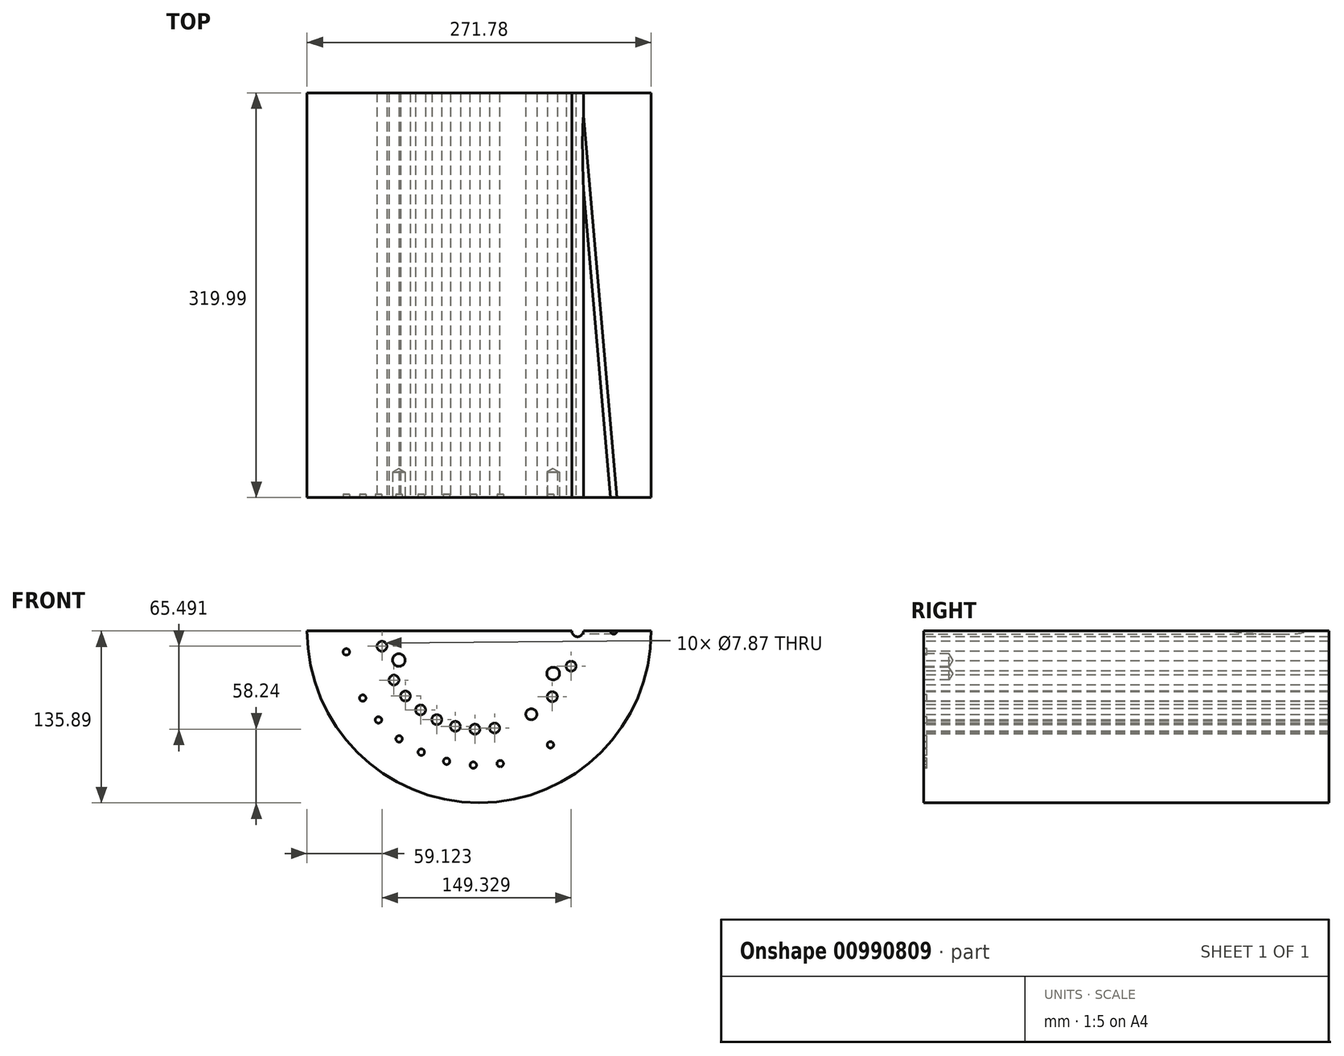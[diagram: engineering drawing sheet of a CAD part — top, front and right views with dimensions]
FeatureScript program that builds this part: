
annotation { "Feature Type Name" : "Feature", "Feature Type Description" : "" }
export const myFeature = defineFeature(function(context is Context, id is Id, definition is map)
    precondition{}
    {
        {
            var Q0;
            Q0=qCreatedBy(makeId("Front.planeOp"),FACE);
            var sketch = newSketch(context, id + "F0", { "sketchPlane" : qUnion([Q0])});
            skCircle(sketch, "E0", {"center": v(0, 0) * mm, "radius": 135.9 * mm});
            skSolve(sketch);
        }
        {
            var Q0;
            Q0 = qSketchRegion(id + "F0", true);
            var Q1;
            Q1 = qSketchRegion(id + "F21", true);
            extrude(context, id + "F1", {"entities" : qUnion([Q0, Q1]), "depth" : 1289.3 * mm, "offsetDistance" : 25.4 * mm});
        }
        {
            var Q0;
            Q0=makeQuery(id+"F1.opExtrude","CAP_FACE",FACE,{"disambiguationData":[OSD([sQuery(id+"F0.wireOp",EDGE,"E0")])],"isStart":false});
            var sketch = newSketch(context, id + "F2", { "sketchPlane" : qUnion([Q0])});
            skCircle(sketch, "E1", {"center": v(0, 0) * mm, "radius": 87.38 * mm});
            skSolve(sketch);
        }
        {
            var Q0;
            Q0 = qSketchRegion(id + "F2", true);
            extrude(context, id + "F3", {"entities" : qUnion([Q0]), "operationType" : NewBodyOperationType.REMOVE, "oppositeDirection" : true, "depth" : 120.65 * mm, "offsetDistance" : 25.4 * mm});
        }
        {
            var Q0;
            Q0=makeQuery(id+"F1.opExtrude","CAP_FACE",FACE,{"disambiguationData":[OSD([sQuery(id+"F0.wireOp",EDGE,"E0")])],"isStart":false});
            var sketch = newSketch(context, id + "F4", { "sketchPlane" : qUnion([Q0])});
            skCircle(sketch, "E2", {"center": v(0, 0) * mm, "radius": 89.66 * mm});
            skSolve(sketch);
        }
        {
            var Q0;
            Q0 = qSketchRegion(id + "F4", true);
            extrude(context, id + "F5", {"entities" : qUnion([Q0]), "operationType" : NewBodyOperationType.REMOVE, "oppositeDirection" : true, "depth" : 25.4 * mm, "offsetDistance" : 25.4 * mm});
        }
        {
            var Q0;
            Q0=makeQuery(id+"F3.boolean.opBoolean","COPY",EDGE,{"derivedFrom":makeQuery(id+"F3.opExtrude","CAP_EDGE",EDGE,{"disambiguationData":[OSD([sQuery(id+"F2.wireOp",EDGE,"E1")])],"isStart":false})});
            var Q1;
            Q1=makeQuery(id+"F5.boolean.opBoolean","COPY",EDGE,{"derivedFrom":makeQuery(id+"F5.opExtrude","CAP_EDGE",EDGE,{"disambiguationData":[OSD([sQuery(id+"F4.wireOp",EDGE,"E2")])],"isStart":false})});
            fillet(context, id + "F6", {"entities" : qUnion([Q0, Q1]), "radius" : 3.05 * mm, "tangentPropagation" : true, "allowEdgeOverflow" : false});
        }
        {
            var Q0;
            Q0=makeQuery(id+"F3.boolean.opBoolean","COPY",FACE,{"derivedFrom":makeQuery(id+"F3.opExtrude","CAP_FACE",FACE,{"disambiguationData":[OSD([sQuery(id+"F2.wireOp",EDGE,"E1")])],"isStart":false})});
            var sketch = newSketch(context, id + "F7", { "sketchPlane" : qUnion([Q0])});
            skPoint(sketch, "E3", {"position": v(71.61, 0) * mm});
            skPoint(sketch, "E4", {"position": v(32.51, 63.8) * mm});
            skPoint(sketch, "E5", {"position": v(-18.87, 69.08) * mm});
            skPoint(sketch, "E6", {"position": v(-65.18, 42.33) * mm});
            skPoint(sketch, "E7", {"position": v(-70.05, 14.89) * mm});
            skPoint(sketch, "E8", {"position": v(66.86, -25.66) * mm});
            skPoint(sketch, "E9", {"position": v(66.86, 25.66) * mm});
            skPoint(sketch, "E10", {"position": v(53.22, -47.92) * mm});
            skPoint(sketch, "E11", {"position": v(37.95, -60.73) * mm});
            skPoint(sketch, "E12", {"position": v(11.2, -70.73) * mm});
            skPoint(sketch, "E13", {"position": v(-3.12, -71.55) * mm});
            skPoint(sketch, "E14", {"position": v(-17.32, -69.49) * mm});
            skPoint(sketch, "E15", {"position": v(-30.83, -64.64) * mm});
            skPoint(sketch, "E16", {"position": v(-42.37, -57.2) * mm});
            skPoint(sketch, "E17", {"position": v(-53.64, -47.45) * mm});
            skPoint(sketch, "E18", {"position": v(-62.02, -35.8) * mm});
            skPoint(sketch, "E19", {"position": v(-70.73, -11.2) * mm});
            skCircle(sketch, "E20", {"center": v(-65.18, 42.33) * mm, "radius": 3.94 * mm});
            skCircle(sketch, "E21", {"center": v(0, 0) * mm, "radius": 77.72 * mm, "construction": true});
            skLineSegment(sketch, "E22", {"start": v(0, 0) * mm, "end": v(-20.48, 74.98) * mm, "construction": true});
            skLineSegment(sketch, "E23", {"start": v(0, 0) * mm, "end": v(-45.99, 62.66) * mm, "construction": true});
            skLineSegment(sketch, "E24", {"start": v(0, 0) * mm, "end": v(-76.03, 16.16) * mm, "construction": true});
            skLineSegment(sketch, "E25", {"start": v(0, 0) * mm, "end": v(-76.77, -12.16) * mm, "construction": true});
            skLineSegment(sketch, "E26", {"start": v(0, 0) * mm, "end": v(35.29, 69.25) * mm, "construction": true});
            skLineSegment(sketch, "E27", {"start": v(0, 0) * mm, "end": v(72.56, 27.85) * mm, "construction": true});
            skLineSegment(sketch, "E28", {"start": v(0, 0) * mm, "end": v(77.72, 0) * mm, "construction": true});
            skLineSegment(sketch, "E29", {"start": v(0, 0) * mm, "end": v(72.56, -27.85) * mm, "construction": true});
            skLineSegment(sketch, "E30", {"start": v(0, 0) * mm, "end": v(57.76, -52) * mm, "construction": true});
            skLineSegment(sketch, "E31", {"start": v(0, 0) * mm, "end": v(41.19, -65.91) * mm, "construction": true});
            skLineSegment(sketch, "E32", {"start": v(0, 0) * mm, "end": v(12.16, -76.77) * mm, "construction": true});
            skLineSegment(sketch, "E33", {"start": v(0, 0) * mm, "end": v(-3.4, -77.65) * mm, "construction": true});
            skLineSegment(sketch, "E34", {"start": v(0, 0) * mm, "end": v(-18.8, -75.42) * mm, "construction": true});
            skLineSegment(sketch, "E35", {"start": v(0, 0) * mm, "end": v(-33.46, -70.15) * mm, "construction": true});
            skLineSegment(sketch, "E36", {"start": v(0, 0) * mm, "end": v(-46.27, -62.45) * mm, "construction": true});
            skLineSegment(sketch, "E37", {"start": v(0, 0) * mm, "end": v(-58.21, -51.5) * mm, "construction": true});
            skLineSegment(sketch, "E38", {"start": v(0, 0) * mm, "end": v(-67.31, -38.86) * mm, "construction": true});
            skCircle(sketch, "E39", {"center": v(-45.99, 62.66) * mm, "radius": 3.94 * mm});
            skCircle(sketch, "E40", {"center": v(-20.48, 74.98) * mm, "radius": 3.94 * mm});
            skCircle(sketch, "E41", {"center": v(35.29, 69.25) * mm, "radius": 3.94 * mm});
            skCircle(sketch, "E42", {"center": v(72.56, 27.85) * mm, "radius": 3.94 * mm});
            skCircle(sketch, "E43", {"center": v(77.72, 0) * mm, "radius": 4.64 * mm});
            skCircle(sketch, "E44", {"center": v(72.56, -27.85) * mm, "radius": 3.94 * mm});
            skCircle(sketch, "E45", {"center": v(57.76, -52) * mm, "radius": 3.94 * mm});
            skCircle(sketch, "E46", {"center": v(41.19, -65.91) * mm, "radius": 4.38 * mm});
            skCircle(sketch, "E47", {"center": v(12.16, -76.77) * mm, "radius": 3.94 * mm});
            skCircle(sketch, "E48", {"center": v(-3.4, -77.65) * mm, "radius": 3.94 * mm});
            skCircle(sketch, "E49", {"center": v(-18.8, -75.42) * mm, "radius": 3.94 * mm});
            skCircle(sketch, "E50", {"center": v(-33.46, -70.15) * mm, "radius": 3.94 * mm});
            skCircle(sketch, "E51", {"center": v(-46.27, -62.45) * mm, "radius": 3.94 * mm});
            skCircle(sketch, "E52", {"center": v(-58.21, -51.5) * mm, "radius": 3.94 * mm});
            skCircle(sketch, "E53", {"center": v(-67.31, -38.86) * mm, "radius": 3.94 * mm});
            skCircle(sketch, "E54", {"center": v(-76.77, -12.16) * mm, "radius": 3.94 * mm});
            skCircle(sketch, "E55", {"center": v(-76.03, 16.16) * mm, "radius": 3.94 * mm});
            skSolve(sketch);
        }
        {
            var Q0;
            Q0 = qSketchRegion(id + "F7", true);
            extrude(context, id + "F8", {"entities" : qUnion([Q0]), "operationType" : NewBodyOperationType.REMOVE, "oppositeDirection" : true, "depth" : 762 * mm, "offsetDistance" : 25.4 * mm});
        }
        {
            var Q0;
            Q0 = qSketchRegion(id + "F7", true);
            extrude(context, id + "F9", {"entities" : qUnion([Q0]), "operationType" : NewBodyOperationType.REMOVE, "oppositeDirection" : true, "depth" : 762 * mm, "offsetDistance" : 25.4 * mm});
        }
        {
            var Q0;
            Q0=makeQuery(id+"F1.opExtrude","CAP_FACE",FACE,{"disambiguationData":[OSD([sQuery(id+"F0.wireOp",EDGE,"E0")])],"isStart":false});
            var sketch = newSketch(context, id + "F10", { "sketchPlane" : qUnion([Q0])});
            skCircle(sketch, "E56", {"center": v(0, 0) * mm, "radius": 50 * mm});
            skCircle(sketch, "E57", {"center": v(0, 0) * mm, "radius": 165.87 * mm});
            skSolve(sketch);
        }
        {
            var Q0;
            Q0 = qSketchRegion(id + "F10", true);
            extrude(context, id + "F11", {"entities" : qUnion([Q0]), "operationType" : NewBodyOperationType.REMOVE, "oppositeDirection" : true, "depth" : 120.65 * mm, "offsetDistance" : 25.4 * mm});
        }
        {
            var Q0;
            Q0 = qSketchRegion(id + "F7", true);
            extrude(context, id + "F12", {"entities" : qUnion([Q0]), "operationType" : NewBodyOperationType.REMOVE, "oppositeDirection" : true, "depth" : 25.4 * mm, "offsetDistance" : 25.4 * mm});
        }
        {
            var Q0;
            Q0=makeQuery(id+"F11.boolean.opBoolean","MERGE",FACE,{"derivedFrom":[makeQuery(id+"F3.boolean.opBoolean","COPY",FACE,{"derivedFrom":makeQuery(id+"F3.opExtrude","CAP_FACE",FACE,{"disambiguationData":[OSD([sQuery(id+"F2.wireOp",EDGE,"E1")])],"isStart":false})})],"fromTools":[makeQuery(id+"F11.opExtrude","CAP_FACE",FACE,{"disambiguationData":[OSD([sQuery(id+"F10.wireOp",EDGE,"E56"),sQuery(id+"F10.wireOp",EDGE,"E57")])],"isStart":false})]});
            var sketch = newSketch(context, id + "F13", { "sketchPlane" : qUnion([Q0])});
            skCircle(sketch, "E58", {"center": v(0, 0) * mm, "radius": 67.5 * mm});
            skPoint(sketch, "E59", {"position": v(0, 67.5) * mm});
            skPoint(sketch, "E60", {"position": v(58.46, -33.75) * mm});
            skPoint(sketch, "E61", {"position": v(-63.43, -23.09) * mm});
            skLineSegment(sketch, "E62", {"start": v(-63.43, -23.09) * mm, "end": v(0, 0) * mm});
            skLineSegment(sketch, "E63", {"start": v(0, 0) * mm, "end": v(0, 67.5) * mm});
            skLineSegment(sketch, "E64", {"start": v(0, 0) * mm, "end": v(58.46, -33.75) * mm});
            skSolve(sketch);
        }
        {
            var Q0;
            Q0=sQuery(id+"F13.wireOp",VERTEX,"E59");
            var Q1;
            Q1=sQuery(id+"F13.wireOp",VERTEX,"E60");
            var Q2;
            Q2=sQuery(id+"F13.wireOp",VERTEX,"E61");
            var Q3;
            Q3=makeQuery(id+"F1.opExtrude","SWEPT_BODY",BODY,{"disambiguationData":[OSD([sQuery(id+"F0.wireOp",EDGE,"E0")])]});
            hole(context, id + "F14", {"style" : HoleStyle.SIMPLE, "endStyle" : HoleEndStyle.BLIND, "holeDiameter" : 10 * mm, "majorDiameter" : 6.35 * mm, "holeDepth" : 20 * mm, "isTappedThrough" : true, "tappedDepth" : 12.7 * mm, "tapClearance" : 3, "locations" : qUnion([Q0, Q1, Q2]), "scope" : qUnion([Q3])});
        }
        {
            var Q0;
            Q0=makeQuery(id+"F11.boolean.opBoolean","MERGE",FACE,{"derivedFrom":[makeQuery(id+"F3.boolean.opBoolean","COPY",FACE,{"derivedFrom":makeQuery(id+"F3.opExtrude","CAP_FACE",FACE,{"disambiguationData":[OSD([sQuery(id+"F2.wireOp",EDGE,"E1")])],"isStart":false})})],"fromTools":[makeQuery(id+"F11.opExtrude","CAP_FACE",FACE,{"disambiguationData":[OSD([sQuery(id+"F10.wireOp",EDGE,"E56"),sQuery(id+"F10.wireOp",EDGE,"E57")])],"isStart":false})]});
            var sketch = newSketch(context, id + "F15", { "sketchPlane" : qUnion([Q0])});
            skCircle(sketch, "E65", {"center": v(0, 0) * mm, "radius": 77.72 * mm, "construction": true});
            skPoint(sketch, "E66.orphan", {"position": v(72.56, 27.85) * mm});
            skPoint(sketch, "E67.orphan", {"position": v(35.29, 69.25) * mm});
            skPoint(sketch, "E68.orphan", {"position": v(-20.48, 74.98) * mm});
            skLineSegment(sketch, "E69", {"start": v(0, 0) * mm, "end": v(-45.99, 62.66) * mm});
            skPoint(sketch, "E70.orphan", {"position": v(-76.03, 16.16) * mm});
            skPoint(sketch, "E71.orphan", {"position": v(-76.77, -12.16) * mm});
            skPoint(sketch, "E72.orphan", {"position": v(-67.31, -38.86) * mm});
            skPoint(sketch, "E73.orphan", {"position": v(-58.21, -51.5) * mm});
            skPoint(sketch, "E74.orphan", {"position": v(-46.27, -62.45) * mm});
            skPoint(sketch, "E75.orphan", {"position": v(-33.46, -70.15) * mm});
            skPoint(sketch, "E76.orphan", {"position": v(-18.8, -75.42) * mm});
            skPoint(sketch, "E77.orphan", {"position": v(-3.4, -77.65) * mm});
            skPoint(sketch, "E78.orphan", {"position": v(12.16, -76.77) * mm});
            skPoint(sketch, "E79.orphan", {"position": v(41.19, -65.91) * mm});
            skPoint(sketch, "E80.orphan", {"position": v(57.76, -52) * mm});
            skPoint(sketch, "E81.orphan", {"position": v(72.56, -27.85) * mm});
            skPoint(sketch, "E82.orphan", {"position": v(77.72, 0) * mm});
            skPoint(sketch, "E83.orphan", {"position": v(-65.18, 42.33) * mm});
            skCircle(sketch, "E84", {"center": v(48.21, 94.62) * mm, "radius": 2.54 * mm});
            skCircle(sketch, "E85", {"center": v(-27.98, 102.45) * mm, "radius": 2.54 * mm});
            skCircle(sketch, "E86", {"center": v(-62.83, 85.61) * mm, "radius": 2.54 * mm});
            skCircle(sketch, "E87", {"center": v(-89.06, 57.84) * mm, "radius": 2.54 * mm});
            skCircle(sketch, "E88", {"center": v(-103.88, 22.08) * mm, "radius": 2.54 * mm});
            skCircle(sketch, "E89", {"center": v(-104.89, -16.61) * mm, "radius": 2.54 * mm});
            skCircle(sketch, "E90", {"center": v(-91.97, -53.1) * mm, "radius": 2.54 * mm});
            skCircle(sketch, "E91", {"center": v(-79.54, -70.37) * mm, "radius": 2.54 * mm});
            skCircle(sketch, "E92", {"center": v(-63.22, -85.33) * mm, "radius": 2.54 * mm});
            skCircle(sketch, "E93", {"center": v(-45.72, -95.85) * mm, "radius": 2.54 * mm});
            skCircle(sketch, "E94", {"center": v(-25.7, -103.04) * mm, "radius": 2.54 * mm});
            skCircle(sketch, "E95", {"center": v(-4.63, -106.1) * mm, "radius": 2.54 * mm});
            skCircle(sketch, "E96", {"center": v(16.61, -104.89) * mm, "radius": 2.54 * mm});
            skCircle(sketch, "E97", {"center": v(56.28, -90.06) * mm, "radius": 2.54 * mm});
            skCircle(sketch, "E98", {"center": v(0, 0) * mm, "radius": 106.2 * mm, "construction": true});
            skSolve(sketch);
        }
        {
            var Q0;
            Q0=qCreatedBy(makeId("Top.planeOp"),FACE);
            var sketch = newSketch(context, id + "F16", { "sketchPlane" : qUnion([Q0])});
            skPoint(sketch, "E99", {"position": v(106.2, -1168.37) * mm});
            skLineSegment(sketch, "E100", {"start": v(106.2, -1168.37) * mm, "end": v(77.42, -839.43) * mm});
            skLineSegment(sketch, "E101", {"start": v(0, -1167.83) * mm, "end": v(0, -1014.52) * mm});
            skLineSegment(sketch, "E102", {"start": v(77.42, -841.85) * mm, "end": v(77.42, -970.13) * mm});
            skLineSegment(sketch, "E103.0", {"start": v(108.73, -1168.15) * mm, "end": v(79.95, -839.2) * mm});
            skLineSegment(sketch, "E104", {"start": v(108.73, -1168.15) * mm, "end": v(108.89, -1169.95) * mm});
            skLineSegment(sketch, "E105", {"start": v(108.89, -1169.95) * mm, "end": v(106.2, -1168.37) * mm});
            skLineSegment(sketch, "E106", {"start": v(77.42, -839.43) * mm, "end": v(79.95, -839.2) * mm});
            skSolve(sketch);
        }
        {
            var Q0;
            Q0=makeQuery(id+"F16.imprint","IMPRINT",FACE,{"disambiguationData":[TD([[makeQuery(id+"F16.imprint","IMPRINT",EDGE,{"derivedFrom":sQuery(id+"F16.wireOp",EDGE,"E100")}),-1.0]])]});
            var Q1;
            Q1=sQuery(id+"F16.wireOp",EDGE,"E100");
            revolve(context, id + "F17", {"operationType" : NewBodyOperationType.REMOVE, "surfaceOperationType" : NewSurfaceOperationType.NEW, "entities" : qUnion([Q0]), "axis" : qUnion([Q1]), "revolveType" : RevolveType.FULL, "oppositeDirection" : true});
        }
        {
            var Q0;
            Q0=qCreatedBy(makeId("Front.planeOp"),FACE);
            var sketch = newSketch(context, id + "F18", { "sketchPlane" : qUnion([Q0])});
            skLineSegment(sketch, "E107", {"start": v(0, 0) * mm, "end": v(-149.71, 0) * mm});
            skLineSegment(sketch, "E108", {"start": v(-149.71, 0) * mm, "end": v(-120.53, 146.7) * mm});
            skLineSegment(sketch, "E109", {"start": v(-120.53, 146.7) * mm, "end": v(24.53, 170.58) * mm});
            skLineSegment(sketch, "E110", {"start": v(24.53, 170.58) * mm, "end": v(135.08, 100.7) * mm});
            skLineSegment(sketch, "E111", {"start": v(135.08, 100.7) * mm, "end": v(164.27, 35.26) * mm});
            skLineSegment(sketch, "E112", {"start": v(164.27, 35.26) * mm, "end": v(164.27, 0) * mm});
            skLineSegment(sketch, "E113", {"start": v(164.27, 0) * mm, "end": v(0, 0) * mm});
            skSolve(sketch);
        }
        {
            var Q0;
            Q0 = qSketchRegion(id + "F18", true);
            extrude(context, id + "F19", {"entities" : qUnion([Q0]), "operationType" : NewBodyOperationType.REMOVE, "depth" : 1292.86 * mm, "offsetDistance" : 25.4 * mm});
        }
        {
            var Q0;
            Q0 = qSketchRegion(id + "F15", true);
            extrude(context, id + "F20", {"entities" : qUnion([Q0]), "operationType" : NewBodyOperationType.REMOVE, "oppositeDirection" : true, "depth" : 2.54 * mm, "offsetDistance" : 25.4 * mm});
        }
        {
            var Q0;
            Q0=makeQuery(id+"F1.opExtrude","CAP_FACE",FACE,{"disambiguationData":[OSD([sQuery(id+"F0.wireOp",EDGE,"E0")])],"isStart":true});
            var sketch = newSketch(context, id + "F21", { "sketchPlane" : qUnion([Q0])});
            skCircle(sketch, "E114", {"center": v(0, 0) * mm, "radius": 180.92 * mm});
            skSolve(sketch);
        }
        {
            var Q0;
            Q0 = qSketchRegion(id + "F21", true);
            extrude(context, id + "F22", {"entities" : qUnion([Q0]), "operationType" : NewBodyOperationType.REMOVE, "oppositeDirection" : true, "depth" : 848.66 * mm, "offsetDistance" : 25.4 * mm});
        }
    });
